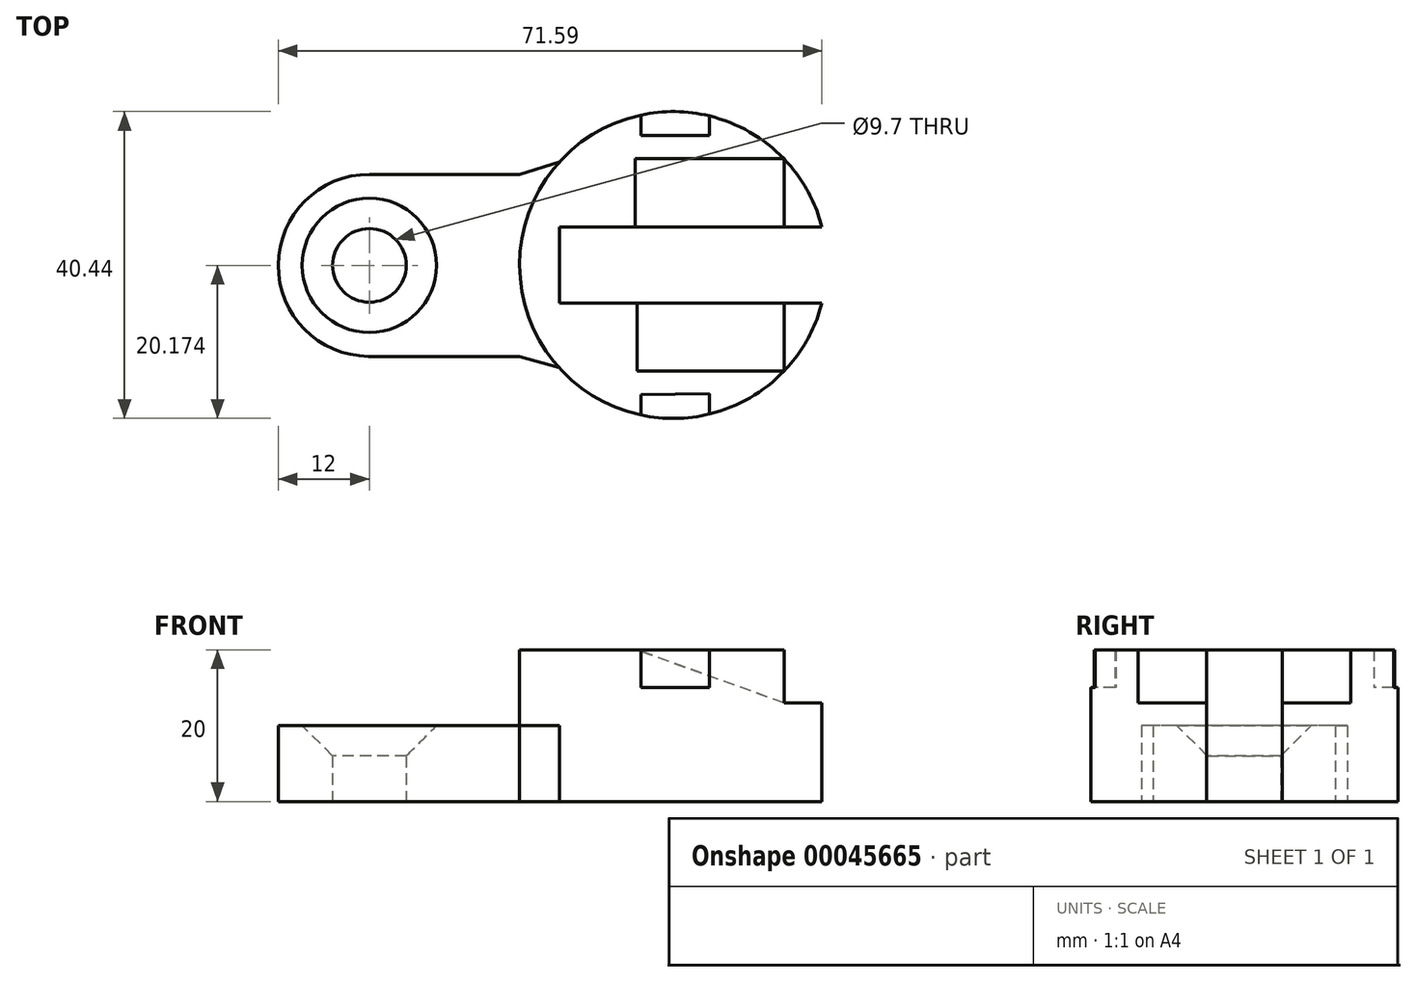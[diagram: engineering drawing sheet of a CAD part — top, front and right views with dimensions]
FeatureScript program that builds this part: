
annotation { "Feature Type Name" : "Feature", "Feature Type Description" : "" }
export const myFeature = defineFeature(function(context is Context, id is Id, definition is map)
    precondition{}
    {
        {
            var Q0;
            Q0=qCreatedBy(makeId("Top.planeOp"),FACE);
            var sketch = newSketch(context, id + "F0", { "sketchPlane" : qUnion([Q0])});
            skArc(sketch, "E0", {"start": v(19.6, 5) * mm, "mid": v(-20.22, 0) * mm, "end": v(19.6, -5) * mm});
            skLineSegment(sketch, "E1.rect.top", {"start": v(4.76, 17.05) * mm, "end": v(-4.24, 17.05) * mm});
            skLineSegment(sketch, "E1.rect.left", {"start": v(4.76, 19.65) * mm, "end": v(4.76, 17.05) * mm});
            skLineSegment(sketch, "E1.rect.right", {"start": v(-4.24, 19.77) * mm, "end": v(-4.24, 17.05) * mm});
            skLineSegment(sketch, "E2.bottom", {"start": v(4.76, -16.95) * mm, "end": v(-4.24, -17.06) * mm});
            skLineSegment(sketch, "E2.left", {"start": v(4.76, -16.95) * mm, "end": v(4.79, -19.65) * mm});
            skLineSegment(sketch, "E2.right", {"start": v(-4.24, -17.06) * mm, "end": v(-4.21, -19.78) * mm});
            skLineSegment(sketch, "E3.rect.bottom", {"start": v(37.37, -5) * mm, "end": v(-15, -5) * mm});
            skLineSegment(sketch, "E3.rect.top", {"start": v(37.37, 5) * mm, "end": v(-15, 5) * mm});
            skLineSegment(sketch, "E3.rect.left", {"start": v(37.37, -5) * mm, "end": v(37.37, 5) * mm});
            skLineSegment(sketch, "E4", {"start": v(-15, 5) * mm, "end": v(-15, -5) * mm});
            skLineSegment(sketch, "E5", {"start": v(0, 5) * mm, "end": v(0, 14) * mm});
            skLineSegment(sketch, "E6", {"start": v(0, 14) * mm, "end": v(14.6, 14) * mm});
            skLineSegment(sketch, "E7", {"start": v(0, -5) * mm, "end": v(0, -14) * mm});
            skLineSegment(sketch, "E8", {"start": v(0, -14) * mm, "end": v(14.6, -14) * mm});
            skLineSegment(sketch, "E9.rect.bottom", {"start": v(-40.1, -12.05) * mm, "end": v(-20.22, -12.05) * mm});
            skLineSegment(sketch, "E9.rect.top", {"start": v(-40, 11.95) * mm, "end": v(-20.22, 11.95) * mm});
            skArc(sketch, "E10", {"start": v(-40, 11.95) * mm, "mid": v(-52, 0) * mm, "end": v(-40.1, -12.05) * mm});
            skCircle(sketch, "E11", {"center": v(-40, -0.05) * mm, "radius": 7.85 * mm});
            skCircle(sketch, "E12", {"center": v(-40, -0.05) * mm, "radius": 4.85 * mm});
            skPoint(sketch, "E13", {"position": v(-20.22, 0) * mm});
            skLineSegment(sketch, "E14", {"start": v(0, -14) * mm, "end": v(-36.77, -14) * mm, "construction": true});
            skLineSegment(sketch, "E15", {"start": v(0, 14) * mm, "end": v(-37, 14) * mm, "construction": true});
            skFitSpline(sketch, "E16", {"points": [v(-20.22, 11.95) * mm, v(-15, 13.56) * mm], "startDerivative": vector(5.22, 1.6) * mm, "endDerivative": vector(5.22, 1.6) * mm});
            skFitSpline(sketch, "E17", {"points": [v(-20.22, -12.05) * mm, v(-15, -13.56) * mm], "startDerivative": vector(5.22, -1.52) * mm, "endDerivative": vector(5.22, -1.52) * mm});
            skSolve(sketch);
        }
        {
            var Q0;
            Q0=makeQuery(id+"F0.imprint","IMPRINT",FACE,{"disambiguationData":[TD([[makeQuery(id+"F0.imprint","IMPRINT",EDGE,{"derivedFrom":sQuery(id+"F0.wireOp",EDGE,"E1.rect.top")}),1.0]])]});
            extrude(context, id + "F1", {"entities" : qUnion([Q0]), "depth" : 20 * mm});
        }
        {
            var Q0;
            Q0=makeQuery(id+"F0.imprint","IMPRINT",FACE,{"disambiguationData":[TD([[makeQuery(id+"F0.imprint","IMPRINT",EDGE,{"derivedFrom":sQuery(id+"F0.wireOp",EDGE,"E1.rect.top")}),-1.0]])]});
            var Q1;
            Q1=makeQuery(id+"F0.imprint","IMPRINT",FACE,{"disambiguationData":[TD([[makeQuery(id+"F0.imprint","IMPRINT",EDGE,{"derivedFrom":sQuery(id+"F0.wireOp",EDGE,"E2.bottom")}),1.0]])]});
            extrude(context, id + "F2", {"entities" : qUnion([Q0, Q1]), "operationType" : NewBodyOperationType.ADD, "depth" : 15 * mm});
        }
        {
            var Q0;
            {var subQ1=sQuery(id+"F0.wireOp",EDGE,"E5");Q0=makeQuery(id+"F0.imprint","IMPRINT",FACE,{"disambiguationData":[TD([[makeQuery(id+"F0.imprint","IMPRINT",EDGE,{"derivedFrom":subQ1}),-1.0]])]});}
            var Q1;
            {var subQ1=sQuery(id+"F0.wireOp",EDGE,"E7");Q1=makeQuery(id+"F0.imprint","IMPRINT",FACE,{"disambiguationData":[TD([[makeQuery(id+"F0.imprint","IMPRINT",EDGE,{"derivedFrom":subQ1}),1.0]])]});}
            extrude(context, id + "F3", {"entities" : qUnion([Q0, Q1]), "operationType" : NewBodyOperationType.ADD, "depth" : 13 * mm});
        }
        {
            var Q0;
            Q0=qCreatedBy(makeId("Front.planeOp"),FACE);
            cPlane(context, id + "F4", {"entities" : qUnion([Q0]), "cplaneType" : CPlaneType.OFFSET, "offset" : 5 * mm, "width" : 150 * mm, "height" : 150 * mm});
        }
        {
            var Q0;
            Q0=qCreatedBy(id+"F4.planeOp",FACE);
            var sketch = newSketch(context, id + "F5", { "sketchPlane" : qUnion([Q0])});
            skLineSegment(sketch, "E18", {"start": v(19.58, 13) * mm, "end": v(0, 20.08) * mm});
            skLineSegment(sketch, "E19", {"start": v(19.58, 13) * mm, "end": v(0, 13) * mm});
            skLineSegment(sketch, "E20", {"start": v(0, 13) * mm, "end": v(0, 20.08) * mm});
            skSolve(sketch);
        }
        {
            var Q0;
            Q0 = qSketchRegion(id + "F5", true);
            extrude(context, id + "F6", {"entities" : qUnion([Q0]), "operationType" : NewBodyOperationType.ADD, "depth" : 9 * mm});
        }
        {
            var Q0;
            Q0=makeQuery(id+"F6.opExtrude","SWEPT_FACE",FACE,{"disambiguationData":[OSD([sQuery(id+"F5.wireOp",EDGE,"E18")])]});
            var Q1;
            Q1=makeQuery(id+"F6.opExtrude","CAP_EDGE",EDGE,{"disambiguationData":[OSD([sQuery(id+"F5.wireOp",EDGE,"E19")])],"isStart":false});
            sweep(context, id + "F7", {"operationType" : NewBodyOperationType.REMOVE, "profiles" : qUnion([Q0]), "path" : qUnion([Q1])});
        }
        {
            var Q0;
            Q0=qCreatedBy(makeId("Front.planeOp"),FACE);
            cPlane(context, id + "F8", {"entities" : qUnion([Q0]), "cplaneType" : CPlaneType.OFFSET, "offset" : 5 * mm, "oppositeDirection" : true, "width" : 150 * mm, "height" : 150 * mm});
        }
        {
            var Q0;
            Q0=qCreatedBy(id+"F8.planeOp",FACE);
            var sketch = newSketch(context, id + "F9", { "sketchPlane" : qUnion([Q0])});
            skLineSegment(sketch, "E21", {"start": v(19.59, 13) * mm, "end": v(0, 20) * mm});
            skLineSegment(sketch, "E22", {"start": v(0, 20) * mm, "end": v(0, 13) * mm});
            skLineSegment(sketch, "E23", {"start": v(0, 13) * mm, "end": v(19.59, 13) * mm});
            skSolve(sketch);
        }
        {
            var Q0;
            Q0=makeQuery(id+"F9.imprint","IMPRINT",FACE,{"disambiguationData":[TD([[makeQuery(id+"F9.imprint","IMPRINT",EDGE,{"derivedFrom":sQuery(id+"F9.wireOp",EDGE,"E21")}),1.0]])]});
            extrude(context, id + "F10", {"entities" : qUnion([Q0]), "operationType" : NewBodyOperationType.ADD, "oppositeDirection" : true, "depth" : 9 * mm});
        }
        {
            var Q0;
            Q0=makeQuery(id+"F10.opExtrude","SWEPT_FACE",FACE,{"disambiguationData":[OSD([sQuery(id+"F9.wireOp",EDGE,"E21")])]});
            var Q1;
            Q1=makeQuery(id+"F10.opExtrude","CAP_EDGE",EDGE,{"disambiguationData":[OSD([sQuery(id+"F9.wireOp",EDGE,"E23")])],"isStart":false});
            sweep(context, id + "F11", {"operationType" : NewBodyOperationType.REMOVE, "profiles" : qUnion([Q0]), "path" : qUnion([Q1])});
        }
        {
            var Q0;
            {var subQ2=sQuery(id+"F0.wireOp",EDGE,"E9.rect.bottom");Q0=makeQuery(id+"F0.imprint","IMPRINT",FACE,{"disambiguationData":[TD([[makeQuery(id+"F0.imprint","IMPRINT",EDGE,{"derivedFrom":subQ2}),1.0]])]});}
            var Q1;
            Q1=makeQuery(id+"F0.imprint","IMPRINT",FACE,{"disambiguationData":[TD([[makeQuery(id+"F0.imprint","IMPRINT",EDGE,{"derivedFrom":sQuery(id+"F0.wireOp",EDGE,"E11")}),1.0]])]});
            extrude(context, id + "F12", {"entities" : qUnion([Q0, Q1]), "operationType" : NewBodyOperationType.ADD, "depth" : 10 * mm});
        }
        {
            var Q0;
            Q0=makeQuery(id+"F12.opExtrude","CAP_EDGE",EDGE,{"disambiguationData":[OSD([sQuery(id+"F0.wireOp",EDGE,"E12")])],"isStart":false});
            chamfer(context, id + "F13", {"entities" : qUnion([Q0]), "width" : 4 * mm, "tangentPropagation" : true});
        }
    });
